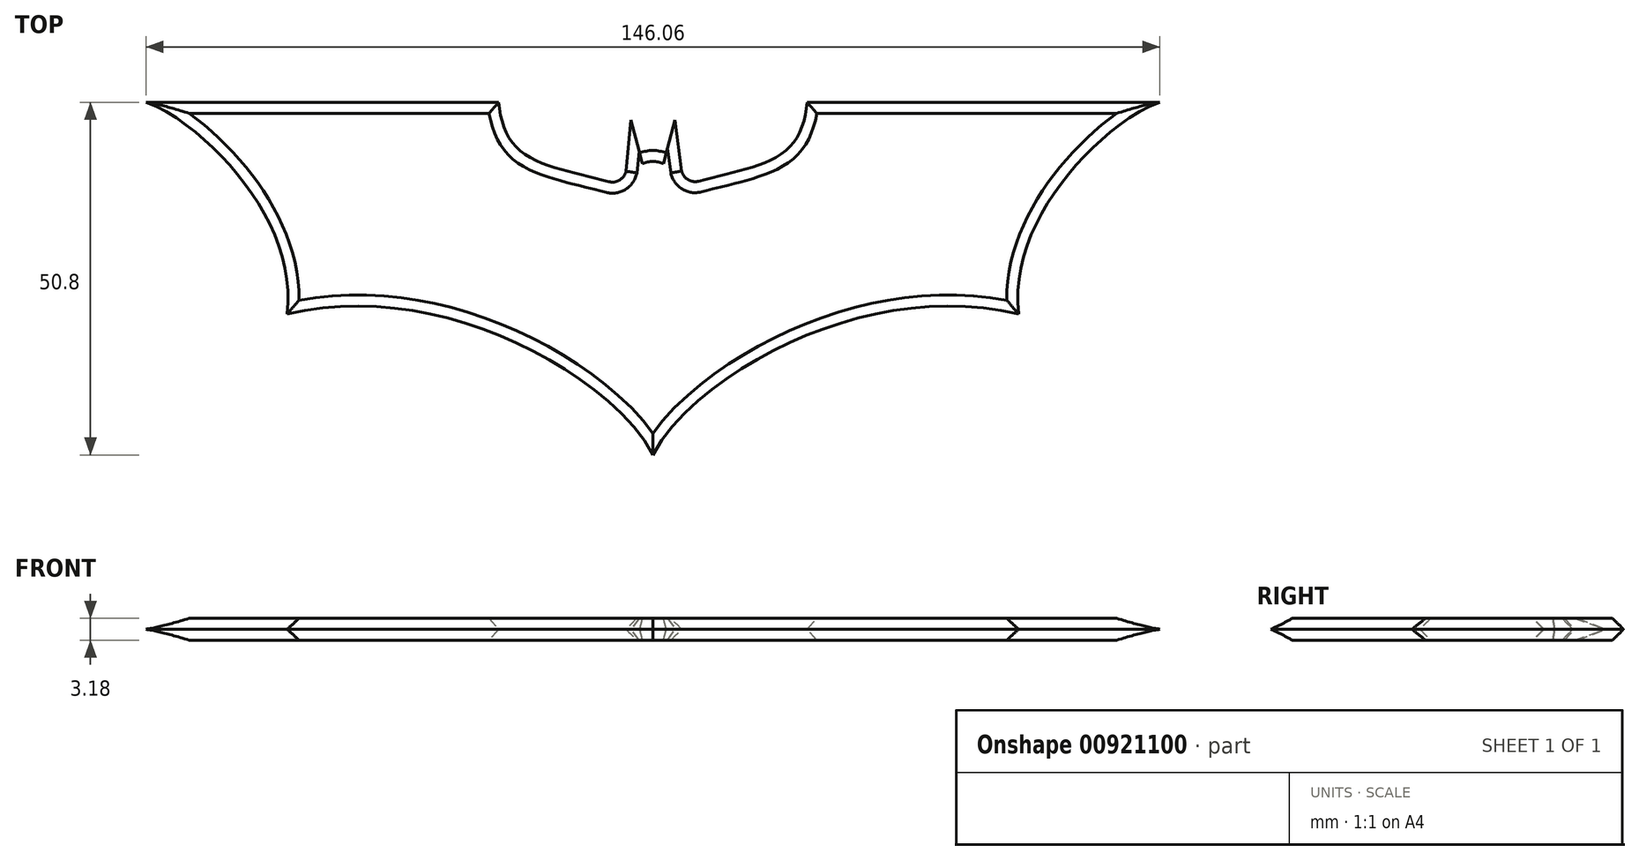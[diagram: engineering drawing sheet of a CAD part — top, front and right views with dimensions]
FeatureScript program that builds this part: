
annotation { "Feature Type Name" : "Feature", "Feature Type Description" : "" }
export const myFeature = defineFeature(function(context is Context, id is Id, definition is map)
    precondition{}
    {
        {
            var Q0;
            Q0=qCreatedBy(makeId("Top.planeOp"),FACE);
            var sketch = newSketch(context, id + "F0", { "sketchPlane" : qUnion([Q0])});
            skLineSegment(sketch, "E0", {"start": v(-73.03, 0) * mm, "end": v(-22.23, 0) * mm});
            skFitSpline(sketch, "E1", {"points": [v(-73.03, 0) * mm, v(-52.7, -30.48) * mm], "startDerivative": vector(19.44, -5.95) * mm, "endDerivative": vector(-5.24, -44.2) * mm});
            skFitSpline(sketch, "E2", {"points": [v(-52.7, -30.48) * mm, v(0, -50.8) * mm], "startDerivative": vector(70.99, 16.7) * mm, "endDerivative": vector(14.25, -29.82) * mm});
            skFitSpline(sketch, "E3", {"points": [v(-22.23, 0) * mm, v(-4.32, -11.98) * mm], "startDerivative": vector(2.79, -27.61) * mm, "endDerivative": vector(33.54, -9.48) * mm});
            skFitSpline(sketch, "E4.MirrorCS", {"points": [v(22.23, 0) * mm, v(4.32, -11.98) * mm], "startDerivative": vector(-2.79, -27.61) * mm, "endDerivative": vector(-33.54, -9.48) * mm});
            skLineSegment(sketch, "E5.MirrorCS", {"start": v(73.03, 0) * mm, "end": v(22.23, 0) * mm});
            skFitSpline(sketch, "E6.MirrorCS", {"points": [v(73.03, 0) * mm, v(52.7, -30.48) * mm], "startDerivative": vector(-19.44, -5.95) * mm, "endDerivative": vector(5.24, -44.2) * mm});
            skFitSpline(sketch, "E7.MirrorCS", {"points": [v(52.7, -30.48) * mm, v(0, -50.8) * mm], "startDerivative": vector(-70.99, 16.7) * mm, "endDerivative": vector(-14.25, -29.82) * mm});
            skLineSegment(sketch, "E8", {"start": v(-52.7, -30.48) * mm, "end": v(-50.34, -10.55) * mm, "construction": true});
            skLineSegment(sketch, "E9", {"start": v(-52.7, -30.48) * mm, "end": v(-31, -25.38) * mm, "construction": true});
            skArc(sketch, "E10.filletArc", {"start": v(-6.34, -11.43) * mm, "mid": v(-4.79, -11.2) * mm, "end": v(-3.88, -9.92) * mm});
            skArc(sketch, "E11.filletArc", {"start": v(4.14, -9.9) * mm, "mid": v(5.06, -11.15) * mm, "end": v(6.6, -11.36) * mm});
            skLineSegment(sketch, "E12.bottom", {"start": v(-22.23, 0) * mm, "end": v(-52.7, 0) * mm, "construction": true});
            skLineSegment(sketch, "E12.top", {"start": v(-22.23, -30.48) * mm, "end": v(-52.7, -30.48) * mm, "construction": true});
            skLineSegment(sketch, "E12.left", {"start": v(-22.23, 0) * mm, "end": v(-22.23, -30.48) * mm, "construction": true});
            skLineSegment(sketch, "E12.right", {"start": v(-52.7, 0) * mm, "end": v(-52.7, -30.48) * mm, "construction": true});
            skLineSegment(sketch, "E13", {"start": v(-22.23, -9.2) * mm, "end": v(-22.23, 0) * mm});
            skLineSegment(sketch, "E14", {"start": v(-3.88, -9.92) * mm, "end": v(-3.14, -2.54) * mm});
            skLineSegment(sketch, "E15", {"start": v(-3.14, -2.54) * mm, "end": v(-1.93, -7.3) * mm});
            skLineSegment(sketch, "E16", {"start": v(4.14, -9.9) * mm, "end": v(3.2, -2.54) * mm});
            skLineSegment(sketch, "E17", {"start": v(3.2, -2.54) * mm, "end": v(1.93, -7.3) * mm});
            skArc(sketch, "E18", {"start": v(1.93, -7.3) * mm, "mid": v(0, -6.94) * mm, "end": v(-1.93, -7.3) * mm});
            skSolve(sketch);
        }
        {
            var Q0;
            Q0=makeQuery(id+"F0.imprint","IMPRINT",FACE,{"disambiguationData":[TD([[makeQuery(id+"F0.imprint","IMPRINT",EDGE,{"derivedFrom":sQuery(id+"F0.wireOp",EDGE,"E0")}),-1.0]])]});
            extrude(context, id + "F1", {"entities" : qUnion([Q0]), "offsetDistance" : 25.4 * mm, "depth" : 3.17 * mm});
        }
        {
            var Q0;
            Q0=makeQuery(id+"F1.opExtrude","CAP_EDGE",EDGE,{"disambiguationData":[OSD([sQuery(id+"F0.wireOp",EDGE,"E2")])],"isStart":false});
            var Q1;
            Q1=makeQuery(id+"F1.opExtrude","CAP_EDGE",EDGE,{"disambiguationData":[OSD([sQuery(id+"F0.wireOp",EDGE,"E1")])],"isStart":false});
            var Q2;
            Q2=makeQuery(id+"F1.opExtrude","CAP_EDGE",EDGE,{"disambiguationData":[OSD([sQuery(id+"F0.wireOp",EDGE,"E7.MirrorCS")])],"isStart":false});
            var Q3;
            Q3=makeQuery(id+"F1.opExtrude","CAP_EDGE",EDGE,{"disambiguationData":[OSD([sQuery(id+"F0.wireOp",EDGE,"E6.MirrorCS")])],"isStart":false});
            var Q4;
            Q4=makeQuery(id+"F1.opExtrude","CAP_EDGE",EDGE,{"disambiguationData":[OSD([sQuery(id+"F0.wireOp",EDGE,"E5.MirrorCS")])],"isStart":false});
            var Q5;
            Q5=makeQuery(id+"F1.opExtrude","CAP_EDGE",EDGE,{"disambiguationData":[OSD([sQuery(id+"F0.wireOp",EDGE,"E0")])],"isStart":false});
            var Q6;
            Q6=makeQuery(id+"F1.opExtrude","CAP_EDGE",EDGE,{"disambiguationData":[OSD([sQuery(id+"F0.wireOp",EDGE,"E3")])],"isStart":false});
            var Q7;
            Q7=makeQuery(id+"F1.opExtrude","CAP_EDGE",EDGE,{"disambiguationData":[OSD([sQuery(id+"F0.wireOp",EDGE,"E14")])],"isStart":false});
            var Q8;
            Q8=makeQuery(id+"F1.opExtrude","CAP_EDGE",EDGE,{"disambiguationData":[OSD([sQuery(id+"F0.wireOp",EDGE,"E4.MirrorCS")])],"isStart":false});
            var Q9;
            Q9=makeQuery(id+"F1.opExtrude","CAP_EDGE",EDGE,{"disambiguationData":[OSD([sQuery(id+"F0.wireOp",EDGE,"E10.filletArc")])],"isStart":false});
            var Q10;
            Q10=makeQuery(id+"F1.opExtrude","CAP_EDGE",EDGE,{"disambiguationData":[OSD([sQuery(id+"F0.wireOp",EDGE,"E11.filletArc")])],"isStart":false});
            var Q11;
            Q11=makeQuery(id+"F1.opExtrude","CAP_EDGE",EDGE,{"disambiguationData":[OSD([sQuery(id+"F0.wireOp",EDGE,"E16")])],"isStart":false});
            var Q12;
            Q12=makeQuery(id+"F1.opExtrude","CAP_EDGE",EDGE,{"disambiguationData":[OSD([sQuery(id+"F0.wireOp",EDGE,"E18")])],"isStart":false});
            chamfer(context, id + "F2", {"entities" : qUnion([Q0, Q1, Q2, Q3, Q4, Q5, Q6, Q7, Q8, Q9, Q10, Q11, Q12]), "width" : 1.59 * mm, "tangentPropagation" : true});
        }
        {
            var Q0;
            Q0=makeQuery(id+"F1.opExtrude","CAP_EDGE",EDGE,{"disambiguationData":[OSD([sQuery(id+"F0.wireOp",EDGE,"E0")])],"isStart":true});
            var Q1;
            Q1=makeQuery(id+"F1.opExtrude","CAP_EDGE",EDGE,{"disambiguationData":[OSD([sQuery(id+"F0.wireOp",EDGE,"E1")])],"isStart":true});
            var Q2;
            Q2=makeQuery(id+"F1.opExtrude","CAP_EDGE",EDGE,{"disambiguationData":[OSD([sQuery(id+"F0.wireOp",EDGE,"E3")])],"isStart":true});
            var Q3;
            Q3=makeQuery(id+"F1.opExtrude","CAP_EDGE",EDGE,{"disambiguationData":[OSD([sQuery(id+"F0.wireOp",EDGE,"E10.filletArc")])],"isStart":true});
            var Q4;
            Q4=makeQuery(id+"F1.opExtrude","CAP_EDGE",EDGE,{"disambiguationData":[OSD([sQuery(id+"F0.wireOp",EDGE,"E16")])],"isStart":true});
            var Q5;
            Q5=makeQuery(id+"F1.opExtrude","CAP_EDGE",EDGE,{"disambiguationData":[OSD([sQuery(id+"F0.wireOp",EDGE,"E11.filletArc")])],"isStart":true});
            var Q6;
            Q6=makeQuery(id+"F1.opExtrude","CAP_EDGE",EDGE,{"disambiguationData":[OSD([sQuery(id+"F0.wireOp",EDGE,"E4.MirrorCS")])],"isStart":true});
            var Q7;
            Q7=makeQuery(id+"F1.opExtrude","CAP_EDGE",EDGE,{"disambiguationData":[OSD([sQuery(id+"F0.wireOp",EDGE,"E2")])],"isStart":true});
            var Q8;
            Q8=makeQuery(id+"F1.opExtrude","CAP_EDGE",EDGE,{"disambiguationData":[OSD([sQuery(id+"F0.wireOp",EDGE,"E7.MirrorCS")])],"isStart":true});
            var Q9;
            Q9=makeQuery(id+"F1.opExtrude","CAP_EDGE",EDGE,{"disambiguationData":[OSD([sQuery(id+"F0.wireOp",EDGE,"E6.MirrorCS")])],"isStart":true});
            var Q10;
            Q10=makeQuery(id+"F1.opExtrude","CAP_EDGE",EDGE,{"disambiguationData":[OSD([sQuery(id+"F0.wireOp",EDGE,"E5.MirrorCS")])],"isStart":true});
            var Q11;
            Q11=makeQuery(id+"F1.opExtrude","CAP_EDGE",EDGE,{"disambiguationData":[OSD([sQuery(id+"F0.wireOp",EDGE,"E18")])],"isStart":true});
            var Q12;
            Q12=makeQuery(id+"F1.opExtrude","CAP_EDGE",EDGE,{"disambiguationData":[OSD([sQuery(id+"F0.wireOp",EDGE,"E14")])],"isStart":true});
            chamfer(context, id + "F3", {"entities" : qUnion([Q0, Q1, Q2, Q3, Q4, Q5, Q6, Q7, Q8, Q9, Q10, Q11, Q12]), "width" : 1.59 * mm, "tangentPropagation" : true});
        }
    });
